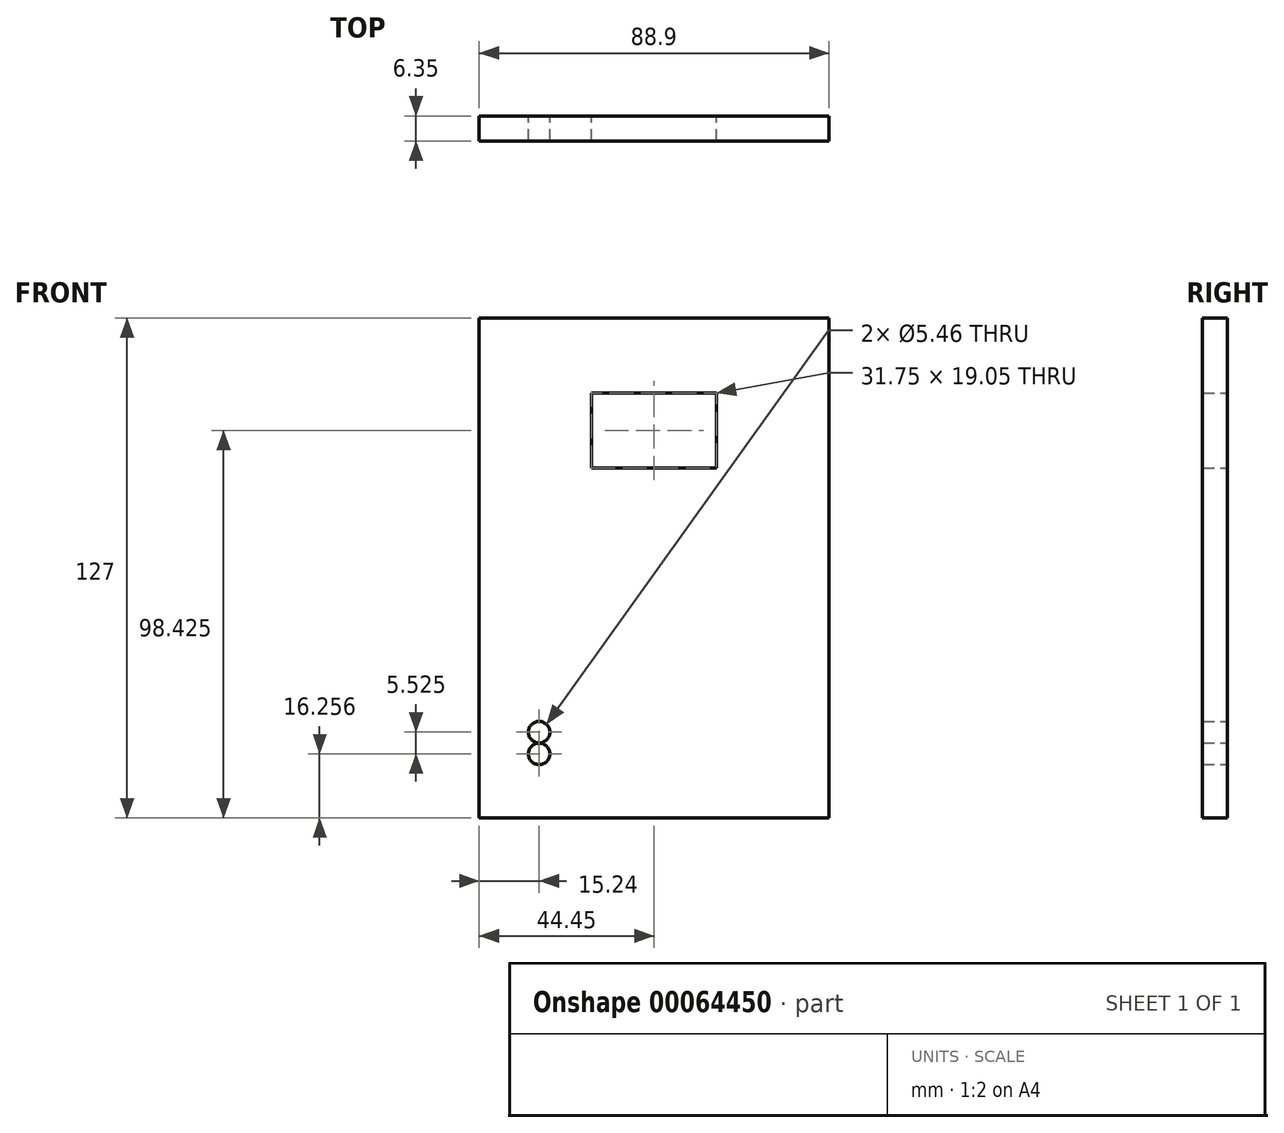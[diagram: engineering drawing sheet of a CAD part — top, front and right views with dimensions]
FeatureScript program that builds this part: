
annotation { "Feature Type Name" : "Feature", "Feature Type Description" : "" }
export const myFeature = defineFeature(function(context is Context, id is Id, definition is map)
    precondition{}
    {
        {
            var Q0;
            Q0=qCreatedBy(makeId("Front.planeOp"),FACE);
            var sketch = newSketch(context, id + "F0", { "sketchPlane" : qUnion([Q0])});
            skLineSegment(sketch, "E0.rect.bottom", {"start": v(44.45, 63.5) * mm, "end": v(-44.45, 63.5) * mm});
            skLineSegment(sketch, "E0.rect.top", {"start": v(44.45, -63.5) * mm, "end": v(-44.45, -63.5) * mm});
            skLineSegment(sketch, "E0.rect.left", {"start": v(44.45, 63.5) * mm, "end": v(44.45, -63.5) * mm});
            skLineSegment(sketch, "E0.rect.right", {"start": v(-44.45, 63.5) * mm, "end": v(-44.45, -63.5) * mm});
            skPoint(sketch, "E0.rect.middle", {"position": v(0, 0) * mm});
            skLineSegment(sketch, "E1.bottom", {"start": v(-15.87, 44.45) * mm, "end": v(15.87, 44.45) * mm});
            skLineSegment(sketch, "E1.top", {"start": v(-15.88, 25.4) * mm, "end": v(15.88, 25.4) * mm});
            skLineSegment(sketch, "E1.left", {"start": v(-15.88, 44.45) * mm, "end": v(-15.87, 25.4) * mm});
            skLineSegment(sketch, "E1.right", {"start": v(15.87, 44.45) * mm, "end": v(15.87, 25.4) * mm});
            skPoint(sketch, "E2", {"position": v(0, 63.5) * mm});
            skPoint(sketch, "E3", {"position": v(0, 44.45) * mm});
            skLineSegment(sketch, "E4", {"start": v(0, 63.5) * mm, "end": v(0, 44.45) * mm, "construction": true});
            skCircle(sketch, "E5", {"center": v(-29.21, -47.24) * mm, "radius": 2.73 * mm});
            skCircle(sketch, "E6", {"center": v(-29.21, -41.72) * mm, "radius": 2.73 * mm});
            skSolve(sketch);
        }
        {
            var Q0;
            Q0 = qSketchRegion(id + "F0", true);
            extrude(context, id + "F1", {"entities" : qUnion([Q0]), "depth" : 6.35 * mm});
        }
    });
